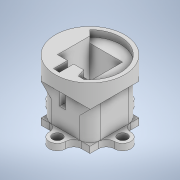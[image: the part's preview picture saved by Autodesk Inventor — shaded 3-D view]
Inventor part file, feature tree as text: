
AUTODESK INVENTOR PART (.ipt)
format: ipt  version: 2022 (Build 260153000, 153)  size: 370,176 bytes
history: native  units: in
note: dims shown in document units (in); Inventor stores cm internally (conversion verified against a paired STEP export)
features: projected_geometry x8, extrude x7, sketch x7, chamfer x2, fillet x2
ambient origin geometry x8: Origin, YZ Plane, XZ Plane, XY Plane, X Axis, Y Axis, Z Axis, Center Point
bodies: Solid1 (feature_tree)
feature tree (26):
  extrude  "Extrusion1"  Depth=0.3986in
  extrude  "Extrusion2"  Depth=0.1in
  extrude  "Extrusion3"  Depth=0.1in
  extrude  "Extrusion4"  Depth=0.315in
  extrude  "Extrusion5"  Depth=0.0787in TaperAngle=0.0deg
  chamfer  "Chamfer4"  Angle=90.0deg  [1 undecoded]
  chamfer  "Chamfer5"  Angle=90.0deg  [1 undecoded]
  extrude  "Extrusion6"  Depth=0.0787in TaperAngle=0.0deg
  fillet  "Fillet2"  [1 undecoded]
  extrude  "Extrusion7"  TaperAngle=90.0deg  [1 undecoded]
  fillet  "Fillet3"  Radius=0.75in
  sketch  "Sketch1"  dims[d0=0.3986in d1=0.3986in]
  sketch  "Sketch2"  dims[d2=0.1in d3=0.1in]
  projected_geometry  "Projected Loop1"
  sketch  "Sketch3"  dims[d4=0.1in d5=0.1in]
  sketch  "Sketch4"  dims[d6=0.315in d7=0.0in d8=0.05in]
  projected_geometry  "Projected Loop2"
  projected_geometry  "Projected Loop3"
  projected_geometry  "Projected Loop4"
  sketch  "Sketch5"  dims[d9=0.4331in d10=0.0in d11=0.0787in d12=0.0in]
  projected_geometry  "Projected Loop5"
  projected_geometry  "Projected Loop6"
  sketch  "Sketch6"  dims[d15=0.1in]
  projected_geometry  "Projected Loop7"
  sketch  "Sketch7"  dims[d16=0.1in d17=90.0deg d18=90.0deg d19=0.0787in d20=0.0in d31=90.0deg d32=90.0deg d33=0.75in d34=0.0787in d35=0.0in d36=0.1239in d37=0.125in d38=45.0deg d39=0.121in d40=0.125in d41=45.0deg d42=0.1in d43=0.2in d44=0.1in d45=0.2in d46=0.1in d47=0.1181in d48=0.1in d49=0.1181in d50=0.0787in d51=0.0in d52=0.1in d53=0.2in d54=0.1in d55=0.1in d56=0.2in d57=0.1in d58=0.1in d59=0.1181in d60=0.1181in d61=0.025in d62=0.0787in d63=0.0in d64=0.125in]
  projected_geometry  "Projected Loop8"
note: 4 required parameter values undecoded (feature->parameter linkage not recoverable at this tier; creation-order binding heuristic only, values carry confidence <= 0.55)
